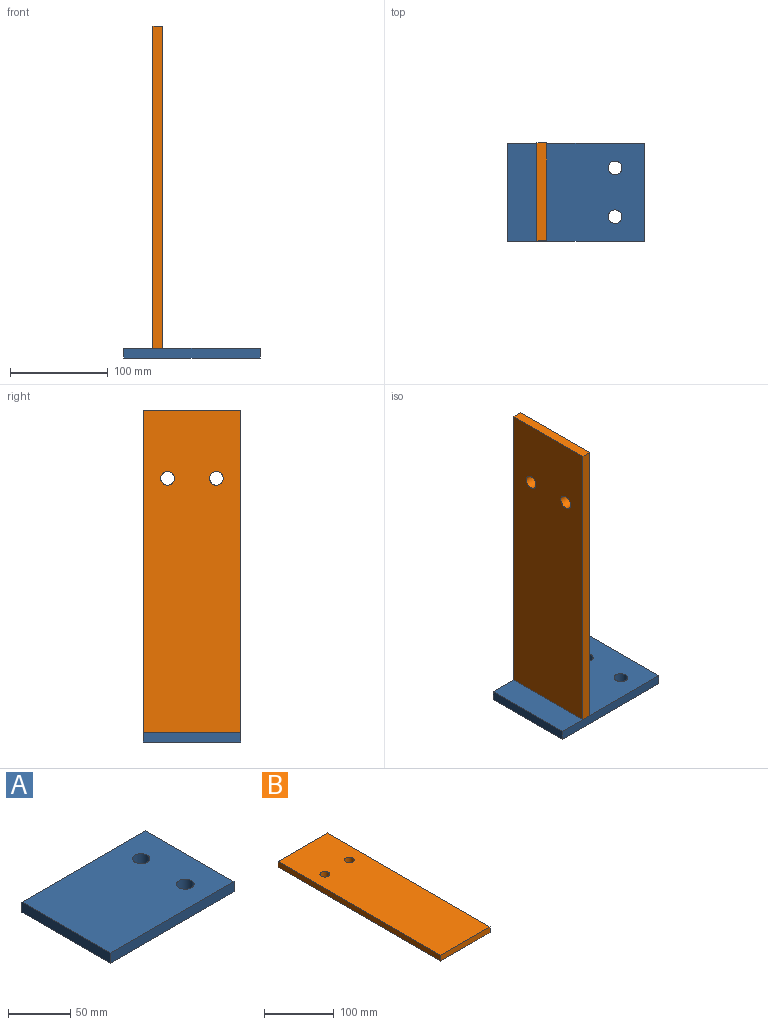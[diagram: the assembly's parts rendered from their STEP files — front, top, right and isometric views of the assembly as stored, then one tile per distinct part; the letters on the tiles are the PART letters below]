
ASSEMBLY  parts=2 mates=1
PART A: 8 faces, bbox 140x100x10 mm
  f0: plane 140x10mm, normal (0,-1,0), area 1400mm2, adj f1,f5,f6,f7
  f1: plane 100x10mm, normal (1,0,0), area 1000mm2, adj f0,f2,f6,f7
  f2: plane 140x10mm, normal (0,1,0), area 1400mm2, adj f1,f5,f6,f7
  f3: cylinder r=7mm len=14mm, axis (0,0,-1), area 439.8mm2, adj f6,f7
  f4: cylinder r=7mm len=14mm, axis (0,0,-1), area 439.8mm2, adj f6,f7
  f5: plane 100x10mm, normal (-1,0,0), area 1000mm2, adj f0,f2,f6,f7
  f6: plane 140x100mm, normal (0,0,1), area 13692.1mm2, adj f0,f1,f2,f3,f4,f5
  f7: plane 140x100mm, normal (0,0,-1), area 13692.1mm2, adj f0,f1,f2,f3,f4,f5
PART B: 8 faces, bbox 100x330x10 mm
  f0: plane 100x10mm, normal (0,-1,0), area 1000mm2, adj f1,f5,f6,f7
  f1: plane 330x10mm, normal (1,0,0), area 3300mm2, adj f0,f2,f6,f7
  f2: plane 100x10mm, normal (0,1,0), area 1000mm2, adj f1,f5,f6,f7
  f3: cylinder r=7mm len=14mm, axis (0,0,-1), area 439.8mm2, adj f6,f7
  f4: cylinder r=7mm len=14mm, axis (0,0,-1), area 439.8mm2, adj f6,f7
  f5: plane 330x10mm, normal (-1,0,0), area 3300mm2, adj f0,f2,f6,f7
  f6: plane 330x100mm, normal (0,0,1), area 32692.1mm2, adj f0,f1,f2,f3,f4,f5
  f7: plane 330x100mm, normal (0,0,-1), area 32692.1mm2, adj f0,f1,f2,f3,f4,f5
PLACE A t=(7.52,3.37,-6.46)mm
PLACE B rot(axis=(0.58,0.58,0.58),120deg) t=(-32.48,3.37,168.54)mm
MATE fastened B.f0 <-> A.f6  axis (0,0,-1) through (-22.48,3.37,3.54)mm
